# Revit family: Bicycle-Racks_Huntco_Morrison
name_source: partatom
category: Site
units: mm (PartAtom-declared; Revit-internal decimal feet)

## family parameters
Classification Number = 23.40.10.11.11
Cut with Voids When Loaded = No
Host = Face
Part Type = Normal
Round Connector Dimension = Use Diameter
Shared = No

## types (2) — shared parameters
Assembly Code = G2040500
Capacity = 1 Bike
Construction Details = http://www.arcat.com
Default Elevation = 0' - 0"
Description = Huntco Wall Mounted Morrison Bike Rack as Specified
Green Building-LEED = http://www.arcat.com
Keynote = 02871
Manufacturer = Huntco Site Furnishings
Manufacturer Fax = 503-274-2055
Manufacturer Website = http://www.huntco.com
Model = Morrison
Product Data = http://www.arcat.com
Revision = R1_2014-09
Sales Information = http://huntco.com
Send Message = http://www.arcat.com
Specification = http://www.arcat.com
URL = http://www.huntco.com
Unit Depth = 0' - 8 1/8"
Unit Height = 1' - 3 3/4"
Unit Width = 0' - 5"
zero-valued in all types: Expected Lifespan (Years), Maintenance Schedule (Months), Warranty Duration (Years)

## per-type parameters (varying)
| type | Include Cable |
| With Cable | Yes |
| Without Cable | No |

## geometry (parser evidence)
native form markers: Blend x6, Sweep x2
no freeform markers — native parametric forms only
